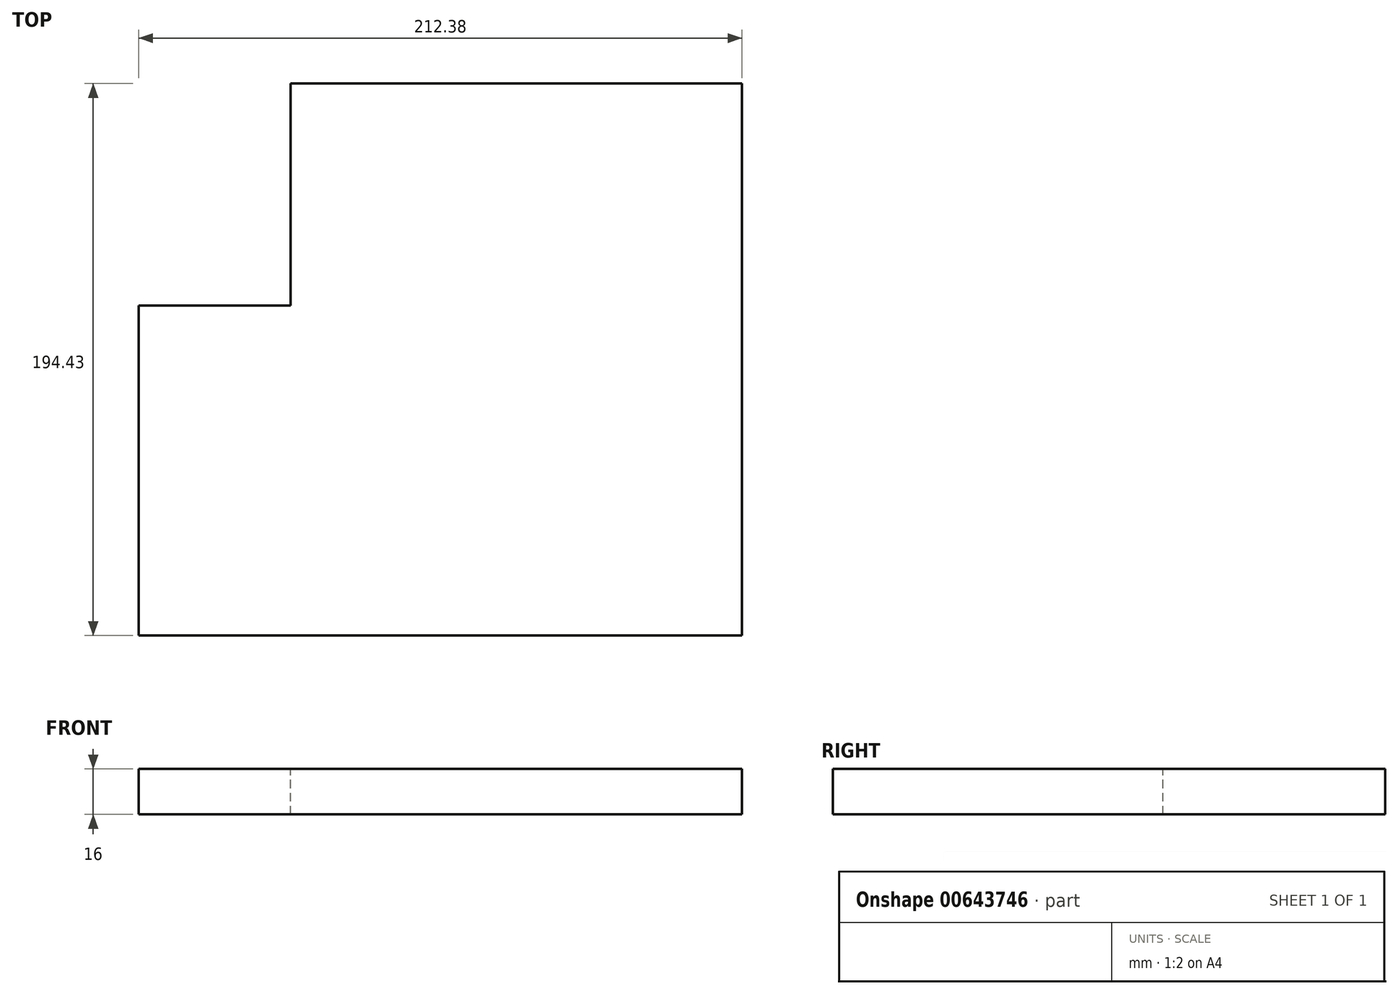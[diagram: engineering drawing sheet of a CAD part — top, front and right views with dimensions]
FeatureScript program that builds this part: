
annotation { "Feature Type Name" : "Feature", "Feature Type Description" : "" }
export const myFeature = defineFeature(function(context is Context, id is Id, definition is map)
    precondition{}
    {
        {
            var Q0;
            Q0=makeQuery(id+"FdyHsF13XDE7NZG.importOp","IMPORT",FACE,{"importTag":0.0});
            cPoint(context, id + "F0", {"pointType" : PointType.MESH_POINT, "mesh" : qUnion([Q0]), "x" : -106.2 * mm, "y" : -97.24 * mm, "z" : -93.51 * mm});
        }
        {
            var Q0;
            Q0=makeQuery(id+"FdyHsF13XDE7NZG.importOp","IMPORT",FACE,{"importTag":0.0});
            cPoint(context, id + "F1", {"pointType" : PointType.MESH_POINT, "mesh" : qUnion([Q0]), "x" : 106.2 * mm, "y" : -97.24 * mm, "z" : -93.51 * mm});
        }
        {
            var Q0;
            Q0=makeQuery(id+"FdyHsF13XDE7NZG.importOp","IMPORT",FACE,{"importTag":0.0});
            cPoint(context, id + "F2", {"pointType" : PointType.MESH_POINT, "mesh" : qUnion([Q0]), "x" : -46.84 * mm, "y" : 97.24 * mm, "z" : -93.51 * mm});
        }
        {
            var Q0;
            Q0 = qCreatedBy(id + "F0" ,VERTEX);
            var Q1;
            Q1 = qCreatedBy(id + "F1" ,VERTEX);
            var Q2;
            Q2 = qCreatedBy(id + "F2" ,VERTEX);
            cPlane(context, id + "F3", {"entities" : qUnion([Q0, Q1, Q2]), "cplaneType" : CPlaneType.THREE_POINT, "offset" : 25 * mm, "width" : 150 * mm, "height" : 150 * mm});
        }
        {
            var Q0;
            Q0=qCreatedBy(id+"F3.planeOp",FACE);
            var sketch = newSketch(context, id + "F4", { "sketchPlane" : qUnion([Q0])});
            skPoint(sketch, "E0.0", {"position": v(106.2, 97.24) * mm});
            skPoint(sketch, "E1.0", {"position": v(-106.2, -18.96) * mm});
            skPoint(sketch, "E2.0", {"position": v(-52.74, -21.96) * mm});
            skPoint(sketch, "E3.0", {"position": v(-55.74, -18.96) * mm});
            skPoint(sketch, "E4.0", {"position": v(101.06, -97.19) * mm});
            skLineSegment(sketch, "E5", {"start": v(106.2, 97.24) * mm, "end": v(106.2, -97.19) * mm});
            skLineSegment(sketch, "E6", {"start": v(101.06, -97.19) * mm, "end": v(-52.74, -97.19) * mm});
            skLineSegment(sketch, "E7", {"start": v(-52.74, -97.19) * mm, "end": v(-52.74, -18.96) * mm});
            skLineSegment(sketch, "E8", {"start": v(-55.74, -18.96) * mm, "end": v(-52.74, -18.96) * mm});
            skLineSegment(sketch, "E9", {"start": v(-55.74, -18.96) * mm, "end": v(-106.2, -18.96) * mm});
            skLineSegment(sketch, "E10", {"start": v(106.2, 97.24) * mm, "end": v(-106.2, 97.24) * mm});
            skLineSegment(sketch, "E11", {"start": v(101.06, -97.19) * mm, "end": v(106.2, -97.19) * mm});
            skLineSegment(sketch, "E12", {"start": v(-106.2, -18.96) * mm, "end": v(-106.2, 97.24) * mm});
            skSolve(sketch);
        }
        {
            var Q0;
            Q0=makeQuery(id+"F4.imprint","IMPRINT",FACE,{"disambiguationData":[TD([[makeQuery(id+"F4.imprint","IMPRINT",EDGE,{"derivedFrom":sQuery(id+"F4.wireOp",EDGE,"E5")}),-1.0]])]});
            extrude(context, id + "F5", {"entities" : qUnion([Q0]), "depth" : 16 * mm, "offsetDistance" : 25 * mm});
        }
    });
